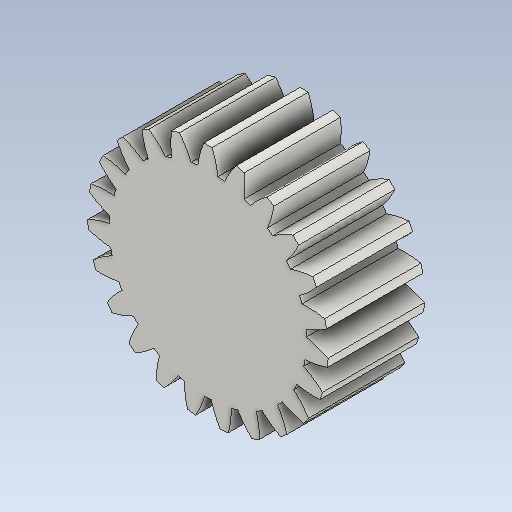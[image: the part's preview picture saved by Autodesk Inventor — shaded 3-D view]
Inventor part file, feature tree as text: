
AUTODESK INVENTOR PART (.ipt)
format: ipt  version: 2021 (Build 250183000, 183)  size: 270,848 bytes
history: native  units: mm (DEFAULTED — no unit token found)
features: plane x3, other x3, sketch x2, extrude x1
ambient origin geometry x8: Origin, YZ Plane, XZ Plane, XY Plane, X Axis, Y Axis, Z Axis, Center Point
bodies: Solid1 (feature_tree)
feature tree (9):
  extrude  "Extrusion1"  Depth=20.0mm TaperAngle=0.0deg
  plane  "Work Plane2"
  plane  "Work Plane8"
  plane  "Work Plane9"
  other  "Engrenage cylindrique"
  sketch  "Sketch1"  dims[d0=50.0mm d1=20.0mm d2=0.0mm]
  sketch  "Sketch2"  dims[d3=46.0mm d4=10.0mm d5=0.0mm d16=80.0mm d17=0.0mm d34=1.36591mm d39=0.0mm d41=0.0mm d43=80.0mm d46=80.0mm d47=0.0mm d48=0.0mm]
  other  "Srf1"
  other  "Diamètre primitif"
